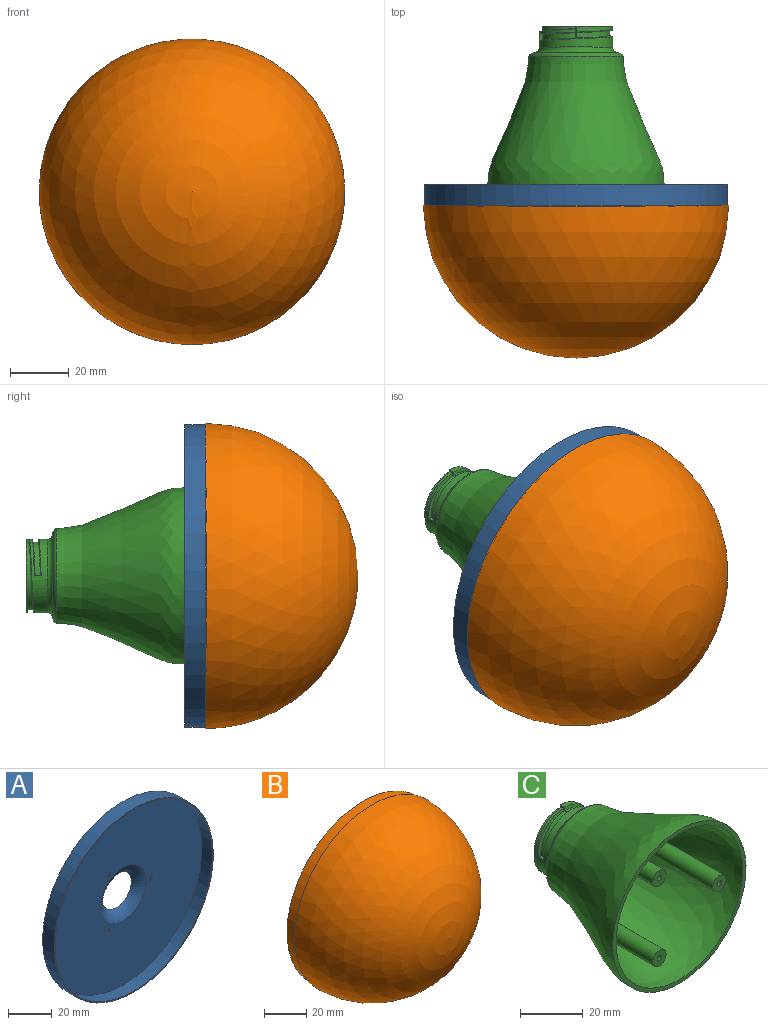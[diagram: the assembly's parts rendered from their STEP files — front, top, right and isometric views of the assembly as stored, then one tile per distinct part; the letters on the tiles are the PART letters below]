
ASSEMBLY  parts=3 mates=3
PART A: 11 faces, bbox 103.2x16.2x103.2 mm
  f0: cylinder r=1mm len=2mm, axis (0,1,0), area 3.8mm2, adj f4,f8
  f1: cylinder r=1mm len=2mm, axis (0,1,0), area 3.8mm2, adj f4,f8
  f2: plane 103.2x103.2mm, normal (0,-1,0), area 193.4mm2, adj f3,f9
  f3: cylinder r=51mm len=102mm, axis (0,-1,0), area 2183.2mm2, adj f2,f4
  f4: plane 102x102mm, normal (0,-1,0), area 7464mm2, adj f0,f1,f3,f5,f10
  f5: torus R=17.92mm, axis (0,-1,0), area 529.6mm2, adj f4,f6
  f6: cone r=9.49mm half-angle=58.9deg, axis (0,1,0), area 36.7mm2, adj f5,f7
  f7: torus R=17.92mm, axis (0,-1,0), area 503.8mm2, adj f6,f8
  f8: plane 103.2x103.2mm, normal (0,1,0), area 7648.4mm2, adj f0,f1,f7,f9,f10
  f9: cylinder r=51.6mm len=103.2mm, axis (0,-1,0), area 2403.4mm2, adj f2,f8
  f10: cylinder r=1mm len=2mm, axis (0,1,0), area 3.8mm2, adj f4,f8
PART B: 6 faces, bbox 104x58x104 mm
  f0: sphere r=49.75mm, area 15551.3mm2, adj f1
  f1: cylinder r=49.75mm len=99.5mm, axis (0,-1,0), area 1875.5mm2, adj f0,f2
  f2: plane 102x102mm, normal (0,1,0), area 395.6mm2, adj f1,f3
  f3: cylinder r=51mm len=102mm, axis (0,-1,0), area 1951.7mm2, adj f2,f4
  f4: plane 104x104mm, normal (0,1,0), area 323.6mm2, adj f3,f5
  f5: sphere r=52mm, area 16960.1mm2, adj f4
PART C: 32 faces, bbox 60.1x54.7x60.1 mm
  f0: cylinder r=12.5mm len=25mm, axis (0,-1,0), area 299.7mm2, adj f1,f2,f7,f26,f29
  f1: bspline ~28.87x25mm, area 96.9mm2, adj f0,f3,f26,f29
  f2: bspline ~18.75x14.43mm, area 19.1mm2, adj f0,f3,f26,f29
  f3: cylinder r=11.5mm len=23mm, axis (0,-1,0), area 152mm2, adj f1,f2,f4,f26,f27,f28,f29,f30
  f4: plane 25.07x24.08mm, normal (0,1,0), area 182.7mm2, adj f3,f6,f13,f27,f28,f29,f31
  f5: revolved ~57x57mm, area 5881.9mm2, adj f11,f12,f14,f17,f18
  f6: cylinder r=12.5mm len=25mm, axis (0,-1,0), area 50.9mm2, adj f4,f27,f28
  f7: torus R=14.5mm, axis (0,-1,0), area 247.5mm2, adj f0,f8
  f8: cone r=14.62mm half-angle=85.7deg, axis (0,-1,0), area 24.5mm2, adj f7,f9
  f9: torus R=14.5mm, axis (0,-1,0), area 191.7mm2, adj f8,f10
  f10: revolved ~60x60mm, area 6629.7mm2, adj f9,f11
  f11: plane 60x60mm, normal (0,-1,0), area 275.9mm2, adj f5,f10
  f12: torus R=13.48mm, axis (0,-1,0), area 503.2mm2, adj f5,f13
  f13: cylinder r=9.5mm len=19mm, axis (0,-1,0), area 426.3mm2, adj f4,f12
  f14: cylinder r=3mm len=38.62mm, axis (0,-1,0), area 541mm2, adj f5,f15
  f15: plane 6x6mm, normal (0,-1,0), area 25.1mm2, adj f14,f25
  f16: plane 6x6mm, normal (0,-1,0), area 25.1mm2, adj f17,f23
  f17: cylinder r=3mm len=38.62mm, axis (0,-1,0), area 541mm2, adj f5,f16
  f18: cylinder r=3mm len=38.62mm, axis (0,-1,0), area 541mm2, adj f5,f19
  f19: plane 6x6mm, normal (0,-1,0), area 25.1mm2, adj f18,f21
  f20: cone r=0mm half-angle=59deg, axis (0,-1,0), area 3.7mm2, adj f21
  f21: cylinder r=1mm len=6mm, axis (0,-1,0), area 37.7mm2, adj f19,f20
  f22: cone r=0mm half-angle=59deg, axis (0,-1,0), area 3.7mm2, adj f23
  f23: cylinder r=1mm len=6mm, axis (0,-1,0), area 37.7mm2, adj f16,f22
  f24: cone r=0mm half-angle=59deg, axis (0,-1,0), area 3.7mm2, adj f25
  f25: cylinder r=1mm len=6mm, axis (0,-1,0), area 37.7mm2, adj f15,f24
  f26: plane 2.3x1mm, normal (0,0,1), area 2.1mm2, adj f0,f1,f2,f3
  f27: bspline ~28.87x25mm, area 52.5mm2, adj f3,f4,f6,f28
  f28: plane 4x1.25mm, normal (-1,0,0), area 3.2mm2, adj f3,f4,f6,f27,f30,f31
  f29: plane 4x1.25mm, normal (1,0,0), area 2.1mm2, adj f0,f1,f2,f3,f4,f30,f31
  f30: plane 0.6x0.25mm, normal (0,1,0), area 0.2mm2, adj f3,f28,f29,f31
  f31: plane 4x0.6mm, normal (0,0,1), area 2.4mm2, adj f4,f28,f29,f30
PLACE A t=(-64.68,-107.68,-23.42)mm
PLACE B t=(-64.68,-108.64,-23.42)mm
PLACE C t=(-64.68,-107.68,-23.42)mm
MATE cylindrical B.f1 <-> A.f3  axis (0,-1,0) through (-64.68,-111.68,-23.42)mm
MATE cylindrical B.f1 <-> A.f3  axis (0,-1,0) through (-64.68,-111.68,-23.42)mm
MATE cylindrical C.f24 <-> A.f10  axis (0,-1,0) through (-46.68,-104.68,-23.42)mm
